# Revit family: QF_ELECTROLUXPROFESSIONAL_1LSNJZ_IC64832FLF_S
name_source: partatom
category: Attrezzature speciali
units: mm (PartAtom-declared; Revit-internal decimal feet)

## family parameters
Basato su piano di lavoro = No
Condiviso = No
Punto di calcolo locali = No
Quota connettore circolare = Usa diametro
Sempre verticale = Sì
Taglio con vuoti quando caricato = No
Tipo di parte = Normale

## types (2) — shared parameters
Cycle = 50 Hz
Depth Actual = 1320 mm
Height Actual = 1460 mm  [stored 4.79003 ft]
Latent Heat Output = 0.0
Length Actual = 3835 mm
Modello = IC64832FLF
Phase = 3
Produttore = Electrolux Professional
Sensible Heat Output = 0.0
Steam Pounds per Hour = 141
URL = www.electroluxprofessional.com
Volts = 400 V
Watts = 1750 W
Weight = 1330
zero-valued in all types: Gas KW, Prospetto di default

## per-type parameters (varying)
| type | Descrizione | Item Number |
| 9882030190 | IRONER CYLINDER IC64832FLF FEEDING+LENGTH FOLDING 3170MM SUPERIOR STEAM CE 400/50/3 4MM SST CYL. ML VAC.FEED.TABLE ANTIS | 1L0GSX |
| 9882030296 | IRONER CYLINDER IC64832FLF FEEDING+LENGTH FOLDING 3170MM SUPERIOR STEAM CE 400/50/3 4MM SST CYL. SE, DK, FI VAC.FEED.TAB | 1LM0BJ |

note: [stored X ft] marks values corroborated as IEEE doubles in the binary element streams (Revit-internal decimal feet)

## geometry (parser evidence)
native form markers: Sweep x11
no freeform markers — native parametric forms only
